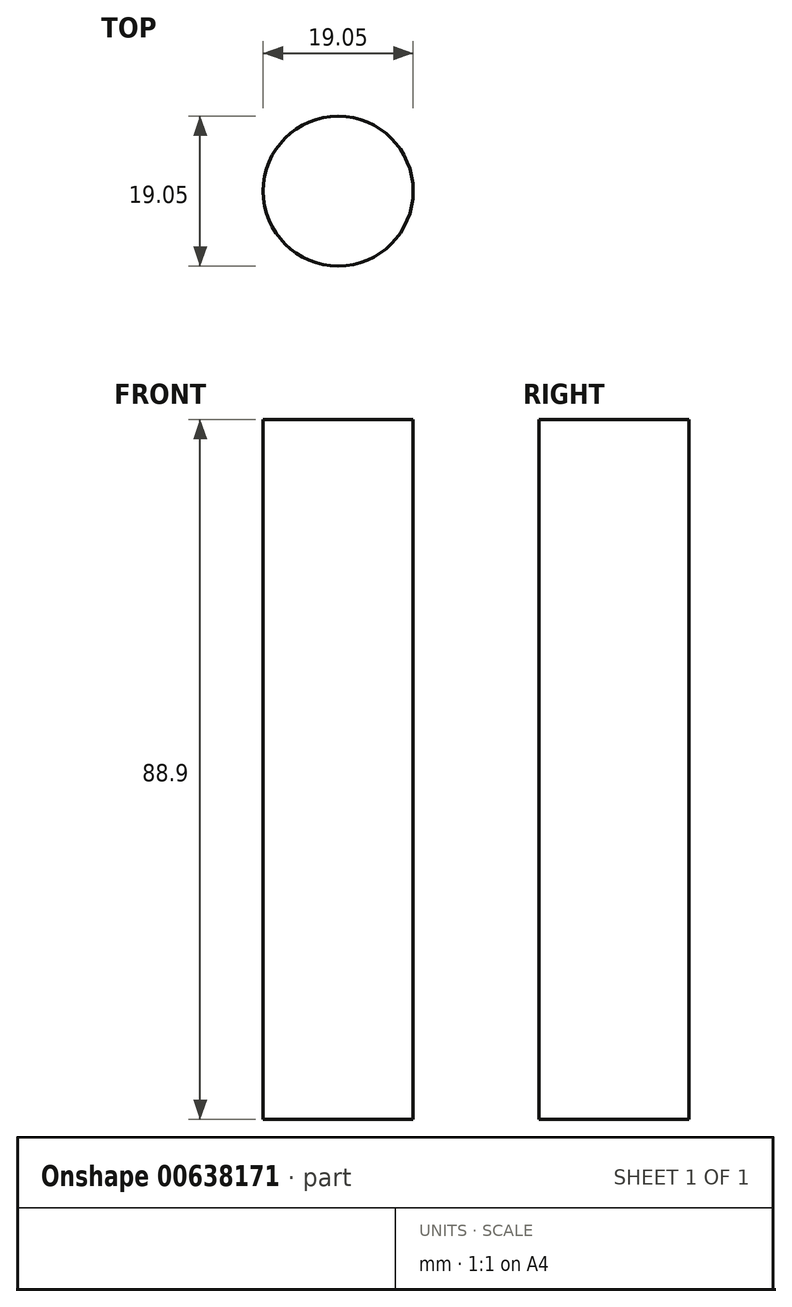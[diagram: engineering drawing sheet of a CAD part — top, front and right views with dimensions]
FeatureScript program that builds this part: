
annotation { "Feature Type Name" : "Feature", "Feature Type Description" : "" }
export const myFeature = defineFeature(function(context is Context, id is Id, definition is map)
    precondition{}
    {
        {
            var Q0;
            Q0=qCreatedBy(makeId("Top.planeOp"),FACE);
            var sketch = newSketch(context, id + "F0", { "sketchPlane" : qUnion([Q0])});
            skCircle(sketch, "E0", {"center": v(-16.01, 9.54) * mm, "radius": 9.53 * mm});
            skSolve(sketch);
        }
        {
            var Q0;
            Q0=makeQuery(id+"F0.imprint","IMPRINT",FACE,{"disambiguationData":[TD([[makeQuery(id+"F0.imprint","IMPRINT",EDGE,{"derivedFrom":sQuery(id+"F0.wireOp",EDGE,"E0")}),1.0]])]});
            extrude(context, id + "F1", {"entities" : qUnion([Q0]), "depth" : 88.9 * mm, "offsetDistance" : 25.4 * mm});
        }
    });
